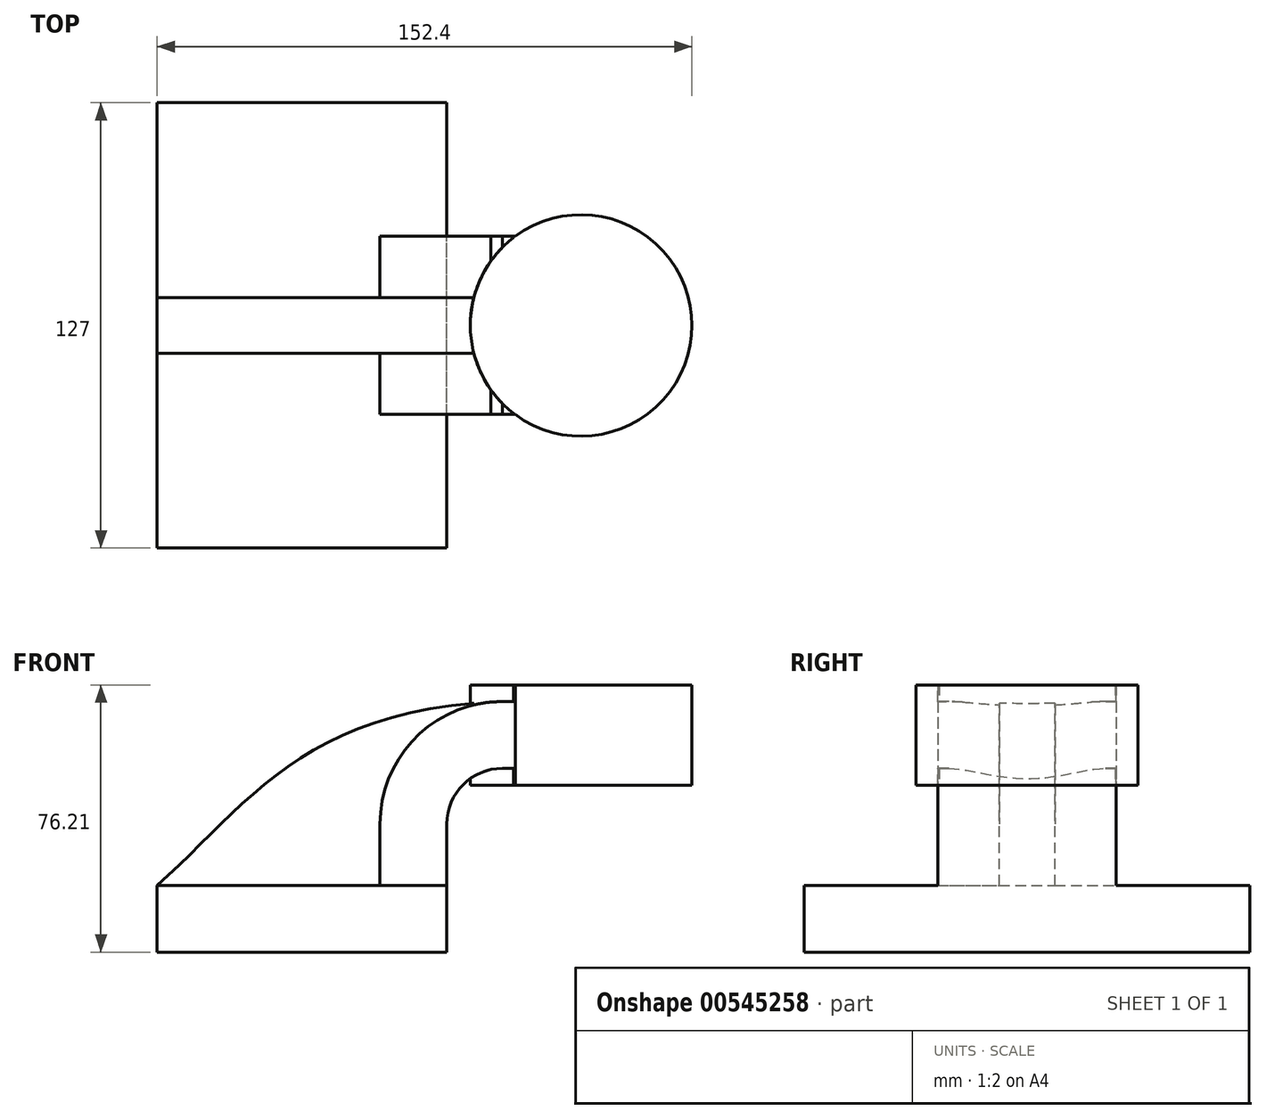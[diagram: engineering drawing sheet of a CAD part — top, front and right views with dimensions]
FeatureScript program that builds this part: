
annotation { "Feature Type Name" : "Feature", "Feature Type Description" : "" }
export const myFeature = defineFeature(function(context is Context, id is Id, definition is map)
    precondition{}
    {
        {
            var Q0;
            Q0=qCreatedBy(makeId("Front.planeOp"),FACE);
            var sketch = newSketch(context, id + "F0", { "sketchPlane" : qUnion([Q0])});
            skLineSegment(sketch, "E0.bottom", {"start": v(-41.28, -9.53) * mm, "end": v(41.28, -9.53) * mm});
            skLineSegment(sketch, "E0.top", {"start": v(-41.28, 9.53) * mm, "end": v(41.28, 9.53) * mm});
            skLineSegment(sketch, "E0.left", {"start": v(-41.28, -9.53) * mm, "end": v(-41.28, 9.53) * mm});
            skLineSegment(sketch, "E0.right", {"start": v(41.28, -9.53) * mm, "end": v(41.28, 9.53) * mm});
            skPoint(sketch, "E0.middle", {"position": v(0, 0) * mm});
            skLineSegment(sketch, "E1.bottom", {"start": v(111.12, 38.1) * mm, "end": v(60.32, 38.1) * mm});
            skLineSegment(sketch, "E1.top", {"start": v(111.12, 66.67) * mm, "end": v(60.33, 66.67) * mm});
            skLineSegment(sketch, "E1.left", {"start": v(111.12, 38.1) * mm, "end": v(111.13, 66.67) * mm});
            skLineSegment(sketch, "E1.right", {"start": v(60.32, 38.1) * mm, "end": v(60.33, 66.67) * mm});
            skPoint(sketch, "E1.middle", {"position": v(85.72, 52.39) * mm});
            skLineSegment(sketch, "E2", {"start": v(41.27, 9.53) * mm, "end": v(41.27, 27) * mm});
            skArc(sketch, "E3", {"start": v(41.27, 27) * mm, "mid": v(45.92, 38.23) * mm, "end": v(57.15, 42.88) * mm});
            skLineSegment(sketch, "E4", {"start": v(57.15, 42.88) * mm, "end": v(79.48, 42.88) * mm});
            skLineSegment(sketch, "E5.0", {"start": v(57.15, 61.93) * mm, "end": v(79.48, 61.93) * mm});
            skArc(sketch, "E5.1", {"start": v(22.23, 27) * mm, "mid": v(32.45, 51.7) * mm, "end": v(57.15, 61.93) * mm});
            skLineSegment(sketch, "E5.2", {"start": v(22.22, 9.53) * mm, "end": v(22.22, 27) * mm});
            skLineSegment(sketch, "E6", {"start": v(79.54, 38.1) * mm, "end": v(79.54, 66.67) * mm});
            skFitSpline(sketch, "E7", {"points": [v(-41.28, 9.53) * mm, v(57.15, 61.93) * mm], "startDerivative": vector(78.53, 69.76) * mm, "endDerivative": vector(171.45, 6.55) * mm});
            skSolve(sketch);
        }
        {
            var Q0;
            {var subQ6=sQuery(id+"F0.wireOp",EDGE,"E6");Q0=makeQuery(id+"F0.imprint","IMPRINT",FACE,{"disambiguationData":[TD([[makeQuery(id+"F0.imprint","IMPRINT",EDGE,{"derivedFrom":subQ6}),1.0]])]});}
            var Q1;
            {var subQ1=sQuery(id+"F0.wireOp",EDGE,"E2");Q1=makeQuery(id+"F0.imprint","IMPRINT",FACE,{"disambiguationData":[TD([[makeQuery(id+"F0.imprint","IMPRINT",EDGE,{"derivedFrom":subQ1}),1.0]])]});}
            extrude(context, id + "F1", {"entities" : qUnion([Q0, Q1]), "endBound" : BoundingType.SYMMETRIC, "depth" : 50.8 * mm, "offsetDistance" : 25.4 * mm});
        }
        {
            var Q0;
            {var subQ3=sQuery(id+"F0.wireOp",EDGE,"E5.2");Q0=makeQuery(id+"F0.imprint","IMPRINT",FACE,{"disambiguationData":[TD([[makeQuery(id+"F0.imprint","IMPRINT",EDGE,{"derivedFrom":subQ3}),1.0]])]});}
            extrude(context, id + "F2", {"entities" : qUnion([Q0]), "operationType" : NewBodyOperationType.ADD, "endBound" : BoundingType.SYMMETRIC, "depth" : 15.88 * mm, "offsetDistance" : 25.4 * mm});
        }
        {
            var Q0;
            {var subQ0=sQuery(id+"F0.wireOp",EDGE,"E1.left");Q0=makeQuery(id+"F0.imprint","IMPRINT",FACE,{"disambiguationData":[TD([[makeQuery(id+"F0.imprint","IMPRINT",EDGE,{"derivedFrom":subQ0}),1.0]])]});}
            var Q1;
            Q1=sQuery(id+"F0.wireOp",EDGE,"E6");
            revolve(context, id + "F3", {"operationType" : NewBodyOperationType.ADD, "entities" : qUnion([Q0]), "axis" : qUnion([Q1]), "revolveType" : RevolveType.FULL});
        }
        {
            var Q0;
            Q0=makeQuery(id+"F0.imprint","IMPRINT",FACE,{"disambiguationData":[TD([[makeQuery(id+"F0.imprint","IMPRINT",EDGE,{"derivedFrom":sQuery(id+"F0.wireOp",EDGE,"E0.bottom")}),1.0]])]});
            extrude(context, id + "F4", {"entities" : qUnion([Q0]), "operationType" : NewBodyOperationType.ADD, "endBound" : BoundingType.SYMMETRIC, "depth" : 127 * mm, "offsetDistance" : 25.4 * mm});
        }
    });
